# Revit family: WAP-Enclosure_NEMA_Ventev_12x10x4-Polycarb
name_source: partatom
category: Generic Models
units: mm (PartAtom-declared; Revit-internal decimal feet)

## family parameters
Always vertical = No
Can host rebar = No
Cut with Voids When Loaded = No
Maintain Annotation Orientation = No
OmniClass Number = 23.85.50.00
OmniClass Title = Communication Systems
Part Type = Normal
Room Calculation Point = No
Round Connector Dimension = Use Diameter
Shared = No
Work Plane-Based = Yes

## types (1)
- WAP-Enclosure_NEMA_Ventev_12x10x4-Polycarb
    Assembly Code = D5030600
    Clear Door = Yes
    Construction Details = http://www.arcat.com
    Default Elevation = 0' - 0"
    Description = Ventev Product as Specified
    Expected Lifespan (Years) = 0
    Hinges = Yes
    Key Lock = Yes
    Keynote = 27 20 00
    Latching = Yes
    Maintenance Schedule (Months) = 0
    Manufacturer = Ventev Innovations
    Manufacturer Website = http://www.terra-wave.com
    Model = As Specified
    Product Data = http://www.arcat.com
    Revision = R1_2016-12
    Sales Information = http://www.terra-wave.com
    Solid Door = Yes
    URL = http://www.terra-wave.com
    Unit Depth = 0' - 5 3/8"
    Unit Height = 1' - 1 11/16"
    Unit Width = 1' - 0 3/16"
    Warranty Duration (Years) = 0

## geometry (parser evidence)
native form markers: Sweep x2
no freeform markers — native parametric forms only
